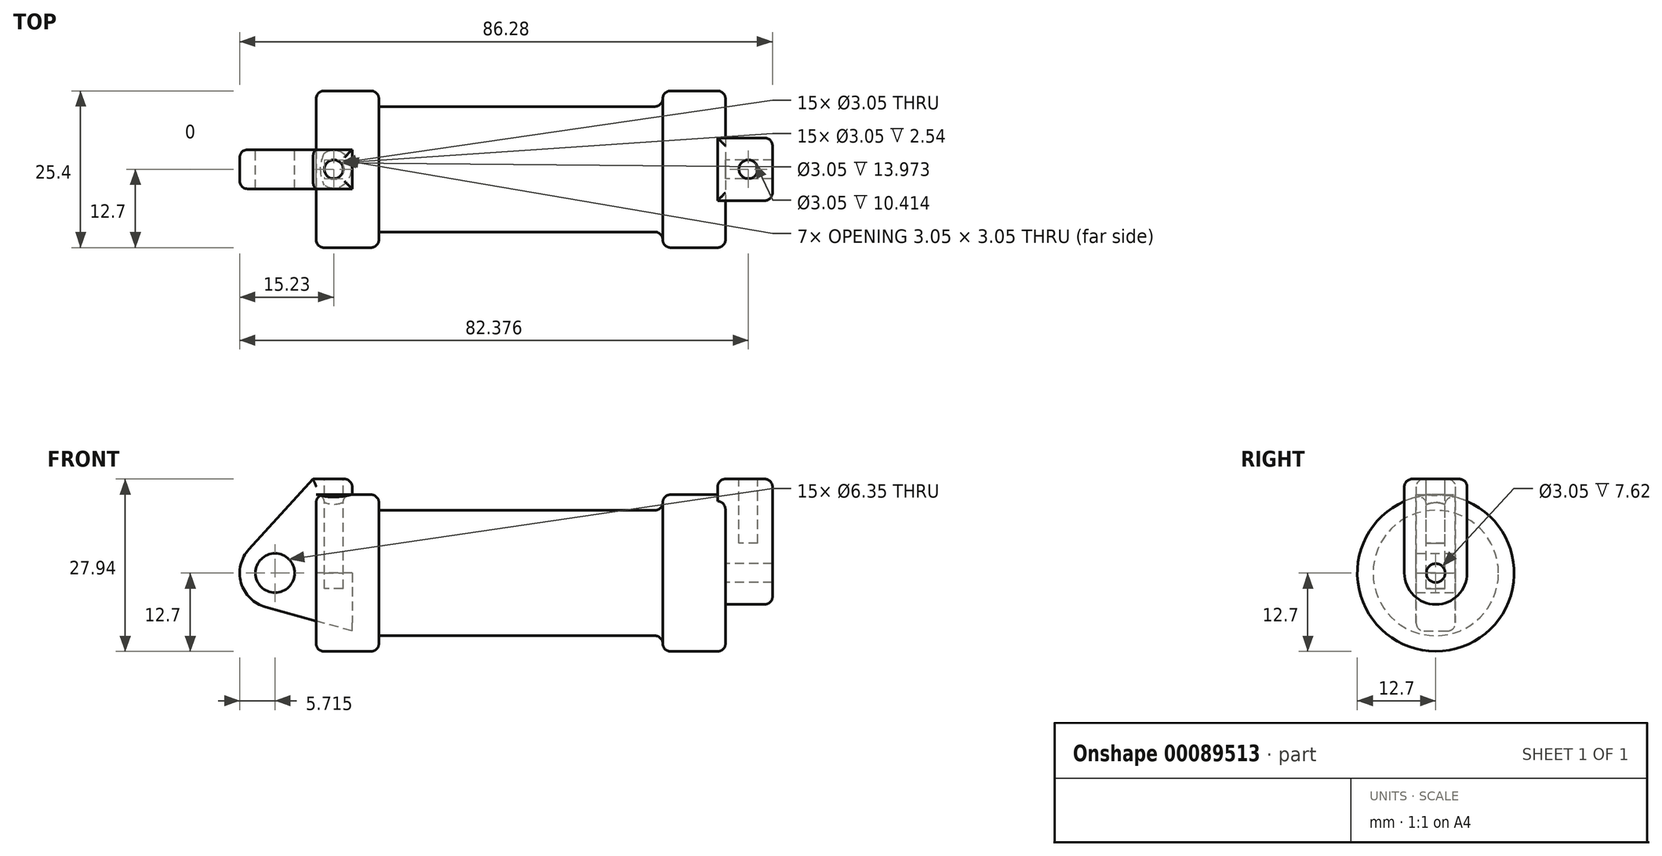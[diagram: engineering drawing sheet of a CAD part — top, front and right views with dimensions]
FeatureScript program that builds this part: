
annotation { "Feature Type Name" : "Feature", "Feature Type Description" : "" }
export const myFeature = defineFeature(function(context is Context, id is Id, definition is map)
    precondition{}
    {
        {
            var Q0;
            Q0=qCreatedBy(makeId("Front.planeOp"),FACE);
            var sketch = newSketch(context, id + "F0", { "sketchPlane" : qUnion([Q0])});
            skLineSegment(sketch, "E0", {"start": v(0, 0) * mm, "end": v(0, 12.7) * mm});
            skLineSegment(sketch, "E1", {"start": v(0, 12.7) * mm, "end": v(10.16, 12.7) * mm});
            skLineSegment(sketch, "E2", {"start": v(10.16, 12.7) * mm, "end": v(10.16, 10.16) * mm});
            skLineSegment(sketch, "E3", {"start": v(10.16, 10.16) * mm, "end": v(56.13, 10.16) * mm});
            skLineSegment(sketch, "E4", {"start": v(56.13, 10.16) * mm, "end": v(56.13, 12.7) * mm});
            skLineSegment(sketch, "E5", {"start": v(56.13, 12.7) * mm, "end": v(66.3, 12.7) * mm});
            skLineSegment(sketch, "E6", {"start": v(66.3, 12.7) * mm, "end": v(66.3, 0) * mm});
            skLineSegment(sketch, "E7", {"start": v(66.3, 0) * mm, "end": v(0, 0) * mm});
            skLineSegment(sketch, "E8", {"start": v(5.84, 15.24) * mm, "end": v(-0.5, 15.24) * mm});
            skLineSegment(sketch, "E9", {"start": v(-0.5, 15.24) * mm, "end": v(-10.88, 3.85) * mm});
            skLineSegment(sketch, "E10", {"start": v(0, 0) * mm, "end": v(-6.65, 0) * mm});
            skCircle(sketch, "E11", {"center": v(-6.65, 0) * mm, "radius": 5.72 * mm});
            skCircle(sketch, "E12", {"center": v(-6.65, 0) * mm, "radius": 3.18 * mm});
            skLineSegment(sketch, "E13", {"start": v(5.84, 15.24) * mm, "end": v(5.84, -9.4) * mm});
            skLineSegment(sketch, "E14", {"start": v(5.84, -9.4) * mm, "end": v(-8.18, -5.5) * mm});
            skSolve(sketch);
        }
        {
            var Q0;
            {var subQ0=sQuery(id+"F0.wireOp",EDGE,"E2");Q0=makeQuery(id+"F0.imprint","IMPRINT",FACE,{"disambiguationData":[TD([[makeQuery(id+"F0.imprint","IMPRINT",EDGE,{"derivedFrom":subQ0}),-1.0]])]});}
            var Q1;
            {var subQ0=sQuery(id+"F0.wireOp",EDGE,"E0");Q1=makeQuery(id+"F0.imprint","IMPRINT",FACE,{"disambiguationData":[TD([[makeQuery(id+"F0.imprint","IMPRINT",EDGE,{"derivedFrom":subQ0}),-1.0]])]});}
            var Q2;
            Q2=sQuery(id+"F0.wireOp",EDGE,"E7");
            revolve(context, id + "F1", {"entities" : qUnion([Q0, Q1]), "axis" : qUnion([Q2]), "revolveType" : RevolveType.FULL});
        }
        {
            var Q0;
            {var subQ3=sQuery(id+"F0.wireOp",EDGE,"E0");Q0=makeQuery(id+"F0.imprint","IMPRINT",FACE,{"disambiguationData":[TD([[makeQuery(id+"F0.imprint","IMPRINT",EDGE,{"derivedFrom":subQ3}),1.0]])]});}
            var Q1;
            {var subQ4=sQuery(id+"F0.wireOp",EDGE,"E12");Q1=makeQuery(id+"F0.imprint","IMPRINT",FACE,{"disambiguationData":[TD([[makeQuery(id+"F0.imprint","IMPRINT",EDGE,{"derivedFrom":subQ4}),-1.0]])]});}
            var Q2;
            {var subQ0=sQuery(id+"F0.wireOp",EDGE,"E14");Q2=makeQuery(id+"F0.imprint","IMPRINT",FACE,{"disambiguationData":[TD([[makeQuery(id+"F0.imprint","IMPRINT",EDGE,{"derivedFrom":subQ0}),-1.0]])]});}
            extrude(context, id + "F2", {"entities" : qUnion([Q0, Q1, Q2]), "endBound" : BoundingType.SYMMETRIC, "depth" : 6.35 * mm});
        }
        {
            var Q0;
            Q0=makeQuery(id+"F1.opRevolve","SWEPT_FACE",FACE,{"disambiguationData":[OSD([sQuery(id+"F0.wireOp",EDGE,"E6")])]});
            var sketch = newSketch(context, id + "F3", { "sketchPlane" : qUnion([Q0])});
            skCircle(sketch, "E15", {"center": v(0, 0) * mm, "radius": 1.52 * mm});
            skCircle(sketch, "E16", {"center": v(0, 0) * mm, "radius": 5.08 * mm});
            skLineSegment(sketch, "E17", {"start": v(-8.24, 15.24) * mm, "end": v(8.24, 15.24) * mm});
            skLineSegment(sketch, "E18", {"start": v(-5.08, 15.24) * mm, "end": v(-5.08, 0) * mm});
            skLineSegment(sketch, "E19", {"start": v(5.08, 15.24) * mm, "end": v(5.08, 0) * mm});
            skSolve(sketch);
        }
        {
            var Q0;
            {var subQ0=sQuery(id+"F3.wireOp",EDGE,"E18");var subQ1=sQuery(id+"F3.wireOp",EDGE,"E17");var subQ2=makeQuery(id+"F3.imprint","INTERSECT",VERTEX,{"derivedFrom":[subQ1,subQ0]});Q0=makeQuery(id+"F3.imprint","IMPRINT",FACE,{"disambiguationData":[TD([[makeQuery(id+"F3.imprint","IMPRINT",EDGE,{"disambiguationData":[TD([[subQ2,-1.0]])],"derivedFrom":subQ1}),-1.0]])]});}
            var Q1;
            {var subQ0=sQuery(id+"F3.wireOp",EDGE,"E18");var subQ1=sQuery(id+"F3.wireOp",EDGE,"E16");var subQ2=makeQuery(id+"F3.imprint","INTERSECT",VERTEX,{"derivedFrom":[subQ1,subQ0]});Q1=makeQuery(id+"F3.imprint","IMPRINT",FACE,{"disambiguationData":[TD([[makeQuery(id+"F3.imprint","IMPRINT",EDGE,{"disambiguationData":[TD([[subQ2,1.0]])],"derivedFrom":subQ1}),-1.0]])]});}
            var Q2;
            Q2=makeQuery(id+"F3.imprint","IMPRINT",FACE,{"disambiguationData":[TD([[makeQuery(id+"F3.imprint","IMPRINT",EDGE,{"derivedFrom":sQuery(id+"F3.wireOp",EDGE,"E15")}),-1.0]])]});
            extrude(context, id + "F4", {"entities" : qUnion([Q0, Q1, Q2]), "operationType" : NewBodyOperationType.ADD, "depth" : 7.62 * mm, "hasSecondDirection" : true, "secondDirectionOppositeDirection" : true, "secondDirectionDepth" : 1.27 * mm});
        }
        {
            var Q0;
            Q0=makeQuery(id+"F2.opExtrude","SWEPT_FACE",FACE,{"disambiguationData":[OSD([sQuery(id+"F0.wireOp",EDGE,"E8")])]});
            var sketch = newSketch(context, id + "F5", { "sketchPlane" : qUnion([Q0])});
            skCircle(sketch, "E20", {"center": v(2.86, 0) * mm, "radius": 1.52 * mm});
            skCircle(sketch, "E21", {"center": v(70, 0) * mm, "radius": 1.52 * mm});
            skSolve(sketch);
        }
        {
            var Q0;
            Q0=makeQuery(id+"F5.imprint","IMPRINT",FACE,{"disambiguationData":[TD([[makeQuery(id+"F5.imprint","IMPRINT",EDGE,{"derivedFrom":sQuery(id+"F5.wireOp",EDGE,"E20")}),1.0]])]});
            extrude(context, id + "F6", {"entities" : qUnion([Q0]), "operationType" : NewBodyOperationType.REMOVE, "oppositeDirection" : true, "depth" : 17.78 * mm});
        }
        {
            var Q0;
            Q0=makeQuery(id+"F5.imprint","IMPRINT",FACE,{"disambiguationData":[TD([[makeQuery(id+"F5.imprint","IMPRINT",EDGE,{"derivedFrom":sQuery(id+"F5.wireOp",EDGE,"E21")}),1.0]])]});
            var Q1;
            Q1=sQuery(id+"F5.wireOp",EDGE,"E21");
            extrude(context, id + "F7", {"entities" : qUnion([Q0]), "operationType" : NewBodyOperationType.REMOVE, "surfaceEntities" : qUnion([Q1]), "oppositeDirection" : true, "depth" : 10.4 * mm});
        }
        {
            var Q0;
            Q0=makeQuery(id+"F1.opRevolve","SWEPT_EDGE",EDGE,{"disambiguationData":[OSD([sQuery(id+"F0.wireOp",EDGE,"E1"),sQuery(id+"F0.wireOp",EDGE,"E2")])]});
            var Q1;
            Q1=makeQuery(id+"F1.opRevolve","SWEPT_FACE",FACE,{"disambiguationData":[OSD([sQuery(id+"F0.wireOp",EDGE,"E1")])]});
            var Q2;
            Q2=makeQuery(id+"F1.opRevolve","SWEPT_EDGE",EDGE,{"disambiguationData":[OSD([sQuery(id+"F0.wireOp",EDGE,"E4"),sQuery(id+"F0.wireOp",EDGE,"E5")])]});
            var Q3;
            Q3=makeQuery(id+"F1.opRevolve","SWEPT_EDGE",EDGE,{"disambiguationData":[OSD([sQuery(id+"F0.wireOp",EDGE,"E5"),sQuery(id+"F0.wireOp",EDGE,"E6")])]});
            var Q4;
            Q4=makeQuery(id+"F4.opExtrude","SWEPT_EDGE",EDGE,{"disambiguationData":[OSD([sQuery(id+"F3.wireOp",EDGE,"E17"),sQuery(id+"F3.wireOp",EDGE,"E19")])]});
            var Q5;
            Q5=makeQuery(id+"F4.opExtrude","CAP_EDGE",EDGE,{"disambiguationData":[OSD([sQuery(id+"F3.wireOp",EDGE,"E17")])],"isStart":true});
            var Q6;
            Q6=makeQuery(id+"F4.opExtrude","SWEPT_EDGE",EDGE,{"disambiguationData":[OSD([sQuery(id+"F3.wireOp",EDGE,"E17"),sQuery(id+"F3.wireOp",EDGE,"E18")])]});
            var Q7;
            Q7=makeQuery(id+"F4.opExtrude","CAP_EDGE",EDGE,{"disambiguationData":[OSD([sQuery(id+"F3.wireOp",EDGE,"E17")])],"isStart":false});
            var Q8;
            Q8=makeQuery(id+"F2.opExtrude","CAP_EDGE",EDGE,{"disambiguationData":[OSD([sQuery(id+"F0.wireOp",EDGE,"E8")])],"isStart":true});
            var Q9;
            Q9=makeQuery(id+"F2.opExtrude","CAP_EDGE",EDGE,{"disambiguationData":[OSD([sQuery(id+"F0.wireOp",EDGE,"E8")])],"isStart":false});
            var Q10;
            Q10=makeQuery(id+"F2.opExtrude","SWEPT_EDGE",EDGE,{"disambiguationData":[OSD([sQuery(id+"F0.wireOp",EDGE,"E8"),sQuery(id+"F0.wireOp",EDGE,"E13")])]});
            var Q11;
            Q11=makeQuery(id+"F2.opExtrude","CAP_EDGE",EDGE,{"disambiguationData":[OSD([sQuery(id+"F0.wireOp",EDGE,"E9")])],"isStart":false});
            var Q12;
            Q12=makeQuery(id+"F2.opExtrude","CAP_EDGE",EDGE,{"disambiguationData":[OSD([sQuery(id+"F0.wireOp",EDGE,"E9")])],"isStart":true});
            var Q13;
            Q13=makeQuery(id+"F2.opExtrude","SWEPT_EDGE",EDGE,{"disambiguationData":[OSD([sQuery(id+"F0.wireOp",EDGE,"E9"),sQuery(id+"F0.wireOp",EDGE,"E11")])]});
            var Q14;
            Q14=makeQuery(id+"F1.opRevolve","SWEPT_EDGE",EDGE,{"disambiguationData":[OSD([sQuery(id+"F0.wireOp",EDGE,"E3"),sQuery(id+"F0.wireOp",EDGE,"E4")])]});
            fillet(context, id + "F8", {"entities" : qUnion([Q0, Q1, Q2, Q3, Q4, Q5, Q6, Q7, Q8, Q9, Q10, Q11, Q12, Q13, Q14]), "radius" : 1.27 * mm, "tangentPropagation" : true, "allowEdgeOverflow" : false});
        }
        {
            var Q0;
            Q0=makeQuery(id+"F4.opExtrude","CAP_EDGE",EDGE,{"disambiguationData":[OSD([sQuery(id+"F3.wireOp",EDGE,"E19")])],"isStart":false});
            var Q1;
            Q1=makeQuery(id+"F4.opExtrude","CAP_EDGE",EDGE,{"disambiguationData":[OSD([sQuery(id+"F3.wireOp",EDGE,"E16")])],"isStart":false});
            var Q2;
            Q2=makeQuery(id+"F4.opExtrude","CAP_EDGE",EDGE,{"disambiguationData":[OSD([sQuery(id+"F3.wireOp",EDGE,"E18")])],"isStart":false});
            var Q3;
            {var subQ0=sQuery(id+"F3.wireOp",EDGE,"E17");Q3=makeQuery(id+"F8.opFillet","BLEND_EDGE",EDGE,{"blendedFrom":[makeQuery(id+"F4.opExtrude","CAP_EDGE",EDGE,{"disambiguationData":[OSD([subQ0])],"isStart":true}),makeQuery(id+"F4.opExtrude","CAP_FACE",FACE,{"disambiguationData":[OSD([sQuery(id+"F3.wireOp",EDGE,"E15"),sQuery(id+"F3.wireOp",EDGE,"E16"),subQ0,sQuery(id+"F3.wireOp",EDGE,"E18"),sQuery(id+"F3.wireOp",EDGE,"E19")])],"isStart":true})],"blendedInto":[makeQuery(id+"F4.opExtrude","CAP_FACE",FACE,{"disambiguationData":[OSD([sQuery(id+"F3.wireOp",EDGE,"E15"),sQuery(id+"F3.wireOp",EDGE,"E16"),subQ0,sQuery(id+"F3.wireOp",EDGE,"E18"),sQuery(id+"F3.wireOp",EDGE,"E19")])],"isStart":true})]});}
            var Q4;
            {var subQ0=sQuery(id+"F3.wireOp",EDGE,"E18");Q4=makeQuery(id+"F8.opFillet","BLEND_EDGE",EDGE,{"blendedFrom":[makeQuery(id+"F4.opExtrude","SWEPT_EDGE",EDGE,{"disambiguationData":[OSD([sQuery(id+"F3.wireOp",EDGE,"E17"),subQ0])]}),makeQuery(id+"F4.opExtrude","SWEPT_FACE",FACE,{"disambiguationData":[OSD([subQ0])]})],"blendedInto":[makeQuery(id+"F4.opExtrude","SWEPT_FACE",FACE,{"disambiguationData":[OSD([subQ0])]})]});}
            fillet(context, id + "F9", {"entities" : qUnion([Q0, Q1, Q2, Q3, Q4]), "radius" : 1.27 * mm, "tangentPropagation" : true, "allowEdgeOverflow" : false});
        }
    });
